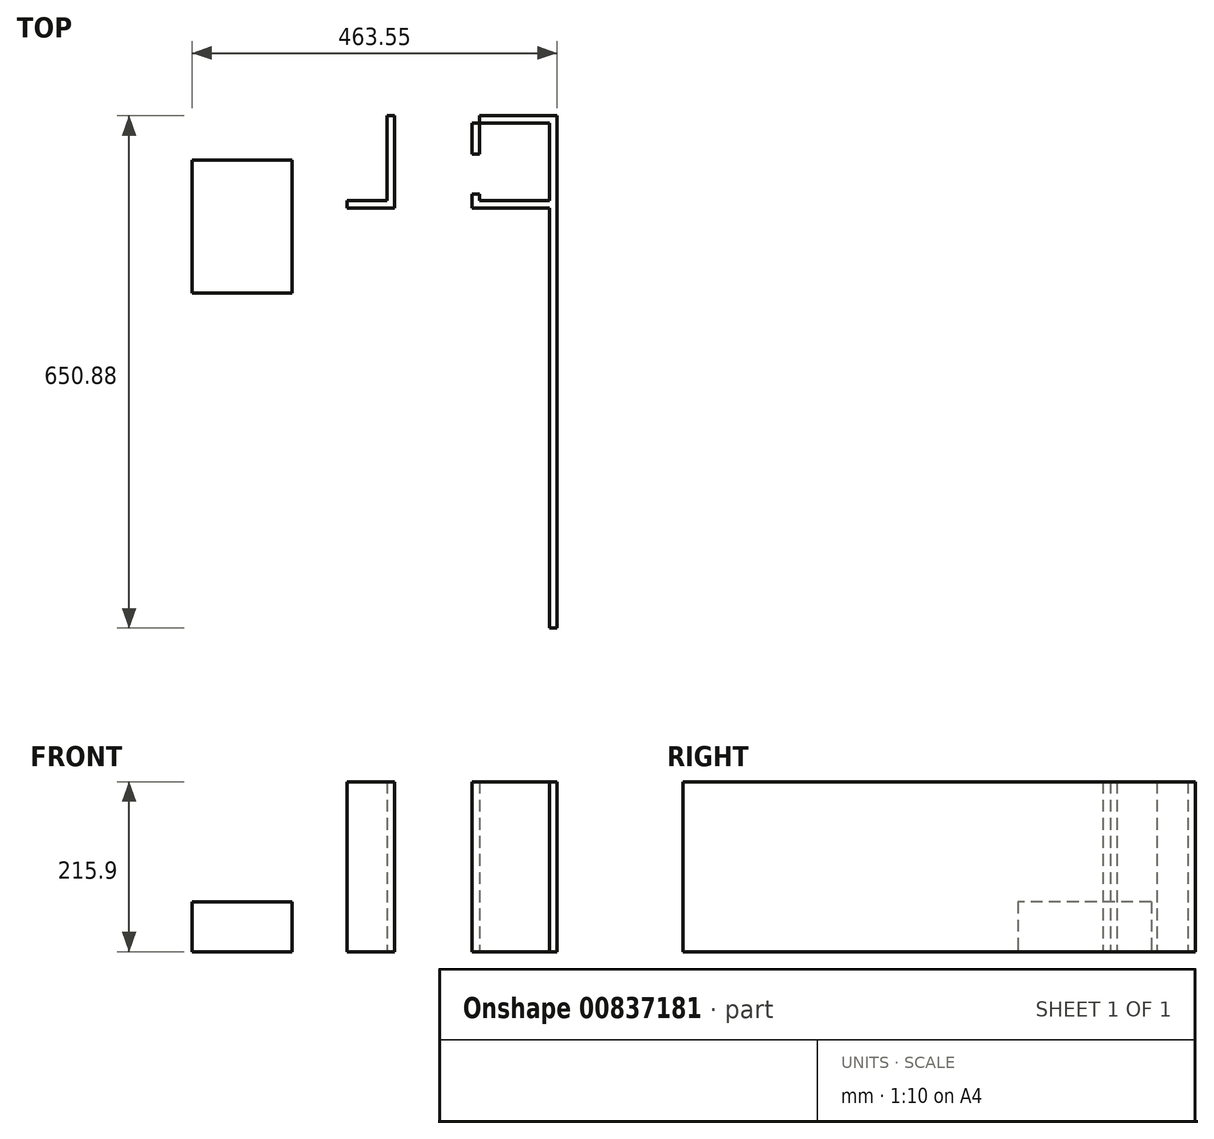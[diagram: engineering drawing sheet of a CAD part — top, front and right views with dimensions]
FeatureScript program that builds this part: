
annotation { "Feature Type Name" : "Feature", "Feature Type Description" : "" }
export const myFeature = defineFeature(function(context is Context, id is Id, definition is map)
    precondition{}
    {
        {
            var Q0;
            Q0=qCreatedBy(makeId("Top.planeOp"),FACE);
            var sketch = newSketch(context, id + "F0", { "sketchPlane" : qUnion([Q0])});
            skLineSegment(sketch, "E0.bottom", {"start": v(0, 0) * mm, "end": v(457.2, 0) * mm});
            skLineSegment(sketch, "E0.left", {"start": v(0, 0) * mm, "end": v(0, 203.2) * mm});
            skLineSegment(sketch, "E1.bottom", {"start": v(0, 0) * mm, "end": v(139.7, 0) * mm});
            skLineSegment(sketch, "E1.top", {"start": v(0, 203.2) * mm, "end": v(139.7, 203.2) * mm});
            skLineSegment(sketch, "E1.left", {"start": v(0, 25.4) * mm, "end": v(0, 203.2) * mm});
            skLineSegment(sketch, "E1.right", {"start": v(139.7, 0) * mm, "end": v(139.7, 25.4) * mm});
            skLineSegment(sketch, "E2.bottom", {"start": v(139.7, 203.2) * mm, "end": v(0, 203.2) * mm});
            skLineSegment(sketch, "E2.top", {"start": v(139.7, 415.93) * mm, "end": v(0, 415.93) * mm});
            skLineSegment(sketch, "E2.left", {"start": v(139.7, 212.72) * mm, "end": v(139.7, 348.2) * mm});
            skLineSegment(sketch, "E2.right", {"start": v(0, 212.72) * mm, "end": v(0, 415.93) * mm});
            skLineSegment(sketch, "E3.bottom", {"start": v(0, 415.93) * mm, "end": v(139.7, 415.93) * mm});
            skLineSegment(sketch, "E3.top", {"start": v(0, 425.45) * mm, "end": v(139.7, 425.45) * mm});
            skLineSegment(sketch, "E4.bottom", {"start": v(139.7, 425.45) * mm, "end": v(0, 425.45) * mm});
            skLineSegment(sketch, "E4.top", {"start": v(139.7, 594.78) * mm, "end": v(0, 594.78) * mm});
            skLineSegment(sketch, "E4.right", {"start": v(0, 425.45) * mm, "end": v(0, 594.78) * mm});
            skLineSegment(sketch, "E5.top", {"start": v(139.7, 212.72) * mm, "end": v(0, 212.72) * mm});
            skLineSegment(sketch, "E6.top", {"start": v(0, 25.4) * mm, "end": v(454.02, 25.4) * mm});
            skLineSegment(sketch, "E6.left", {"start": v(0, 0) * mm, "end": v(0, 25.4) * mm});
            skLineSegment(sketch, "E7.top", {"start": v(0, 0) * mm, "end": v(-9.53, 0) * mm});
            skLineSegment(sketch, "E7.left", {"start": v(0, 594.78) * mm, "end": v(0, 212.72) * mm});
            skLineSegment(sketch, "E7.right", {"start": v(-9.53, 594.78) * mm, "end": v(-9.53, 0) * mm});
            skLineSegment(sketch, "E8.top", {"start": v(0, 594.78) * mm, "end": v(139.7, 594.78) * mm});
            skLineSegment(sketch, "E9.top", {"start": v(-9.53, 604.3) * mm, "end": v(139.7, 604.3) * mm});
            skLineSegment(sketch, "E9.left", {"start": v(-9.53, 594.78) * mm, "end": v(-9.53, 604.3) * mm});
            skLineSegment(sketch, "E10.trimOffspring", {"start": v(139.7, 348.2) * mm, "end": v(139.7, 212.72) * mm});
            skLineSegment(sketch, "E11.trimOffspring", {"start": v(139.7, 25.4) * mm, "end": v(139.7, 0) * mm});
            skLineSegment(sketch, "E12.trimOffspring", {"start": v(0, 212.72) * mm, "end": v(0, 594.78) * mm});
            skLineSegment(sketch, "E13.trimOffspring", {"start": v(0, 203.2) * mm, "end": v(0, 25.4) * mm});
            skLineSegment(sketch, "E14", {"start": v(139.7, 604.3) * mm, "end": v(139.7, 650.88) * mm});
            skLineSegment(sketch, "E15", {"start": v(139.7, 650.88) * mm, "end": v(454.02, 650.88) * mm});
            skLineSegment(sketch, "E16.bottom", {"start": v(454.02, 650.88) * mm, "end": v(463.55, 650.88) * mm});
            skLineSegment(sketch, "E16.top", {"start": v(454.02, 0) * mm, "end": v(463.55, 0) * mm});
            skLineSegment(sketch, "E16.left", {"start": v(454.02, 650.88) * mm, "end": v(454.02, 0) * mm});
            skLineSegment(sketch, "E16.right", {"start": v(463.55, 650.88) * mm, "end": v(463.55, 0) * mm});
            skLineSegment(sketch, "E17.bottom", {"start": v(149.22, 641.35) * mm, "end": v(247.65, 641.35) * mm});
            skLineSegment(sketch, "E17.top", {"start": v(196.85, 542.92) * mm, "end": v(247.65, 542.92) * mm});
            skLineSegment(sketch, "E17.left", {"start": v(149.22, 641.35) * mm, "end": v(149.22, 594.78) * mm});
            skLineSegment(sketch, "E17.right", {"start": v(247.65, 641.35) * mm, "end": v(247.65, 542.93) * mm});
            skLineSegment(sketch, "E18.bottom", {"start": v(454.02, 641.35) * mm, "end": v(355.6, 641.35) * mm});
            skLineSegment(sketch, "E18.top", {"start": v(454.02, 542.93) * mm, "end": v(355.6, 542.93) * mm});
            skLineSegment(sketch, "E18.left", {"start": v(454.02, 641.35) * mm, "end": v(454.02, 542.93) * mm});
            skLineSegment(sketch, "E18.right", {"start": v(355.6, 641.35) * mm, "end": v(355.6, 542.93) * mm});
            skLineSegment(sketch, "E19.top", {"start": v(196.85, 533.4) * mm, "end": v(247.65, 533.4) * mm});
            skLineSegment(sketch, "E19.right", {"start": v(247.65, 542.93) * mm, "end": v(247.65, 533.4) * mm});
            skLineSegment(sketch, "E20.bottom", {"start": v(355.6, 542.93) * mm, "end": v(454.02, 542.93) * mm});
            skLineSegment(sketch, "E20.top", {"start": v(355.6, 533.4) * mm, "end": v(454.02, 533.4) * mm});
            skLineSegment(sketch, "E20.left", {"start": v(355.6, 542.93) * mm, "end": v(355.6, 533.4) * mm});
            skLineSegment(sketch, "E20.right", {"start": v(454.02, 542.93) * mm, "end": v(454.02, 533.4) * mm});
            skLineSegment(sketch, "E21.bottom", {"start": v(247.65, 533.4) * mm, "end": v(257.17, 533.4) * mm});
            skLineSegment(sketch, "E21.top", {"start": v(247.65, 650.88) * mm, "end": v(257.17, 650.88) * mm});
            skLineSegment(sketch, "E21.left", {"start": v(247.65, 533.4) * mm, "end": v(247.65, 650.88) * mm});
            skLineSegment(sketch, "E21.right", {"start": v(257.17, 533.4) * mm, "end": v(257.17, 650.88) * mm});
            skLineSegment(sketch, "E22.bottom", {"start": v(365.12, 533.4) * mm, "end": v(355.6, 533.4) * mm});
            skLineSegment(sketch, "E22.top", {"start": v(365.12, 650.88) * mm, "end": v(355.6, 650.88) * mm});
            skLineSegment(sketch, "E22.left", {"start": v(355.6, 533.4) * mm, "end": v(355.6, 650.88) * mm});
            skLineSegment(sketch, "E22.right", {"start": v(365.12, 533.4) * mm, "end": v(365.12, 650.88) * mm});
            skLineSegment(sketch, "E23", {"start": v(139.7, 425.45) * mm, "end": v(149.22, 425.45) * mm});
            skLineSegment(sketch, "E24", {"start": v(139.7, 415.93) * mm, "end": v(149.22, 415.93) * mm});
            skLineSegment(sketch, "E25", {"start": v(139.7, 348.2) * mm, "end": v(149.22, 348.2) * mm});
            skLineSegment(sketch, "E26", {"start": v(139.7, 177.8) * mm, "end": v(149.22, 177.8) * mm});
            skLineSegment(sketch, "E27.trimOffspring", {"start": v(139.7, 177.8) * mm, "end": v(139.7, 203.2) * mm});
            skLineSegment(sketch, "E28.trimOffspring", {"start": v(149.22, 348.2) * mm, "end": v(149.22, 177.8) * mm});
            skLineSegment(sketch, "E29.trimOffspring", {"start": v(149.22, 425.45) * mm, "end": v(149.22, 415.93) * mm});
            skLineSegment(sketch, "E30", {"start": v(139.7, 594.78) * mm, "end": v(149.22, 594.78) * mm});
            skLineSegment(sketch, "E31", {"start": v(196.85, 542.93) * mm, "end": v(196.85, 533.4) * mm});
            skLineSegment(sketch, "E32.bottom", {"start": v(365.12, 551.4) * mm, "end": v(355.6, 551.4) * mm});
            skLineSegment(sketch, "E32.top", {"start": v(365.12, 602.2) * mm, "end": v(355.6, 602.2) * mm});
            skLineSegment(sketch, "E32.left", {"start": v(365.12, 551.4) * mm, "end": v(365.12, 602.2) * mm});
            skLineSegment(sketch, "E32.right", {"start": v(355.6, 551.4) * mm, "end": v(355.6, 602.2) * mm});
            skSolve(sketch);
        }
        {
            var Q0;
            Q0=makeQuery(id+"F0.imprint","IMPRINT",FACE,{"disambiguationData":[TD([[makeQuery(id+"F0.imprint","IMPRINT",EDGE,{"derivedFrom":sQuery(id+"F0.wireOp",EDGE,"E2.bottom")}),-1.0]])]});
            var Q1;
            {var subQ1=sQuery(id+"F0.wireOp",EDGE,"E3.bottom");Q1=makeQuery(id+"F0.imprint","IMPRINT",FACE,{"disambiguationData":[TD([[makeQuery(id+"F0.imprint","IMPRINT",EDGE,{"derivedFrom":subQ1}),1.0]])]});}
            var Q2;
            {var subQ3=sQuery(id+"F0.wireOp",EDGE,"E21.bottom");Q2=makeQuery(id+"F0.imprint","IMPRINT",FACE,{"disambiguationData":[TD([[makeQuery(id+"F0.imprint","IMPRINT",EDGE,{"derivedFrom":subQ3}),1.0]])]});}
            var Q3;
            {var subQ0=sQuery(id+"F0.wireOp",EDGE,"E17.top");Q3=makeQuery(id+"F0.imprint","IMPRINT",FACE,{"disambiguationData":[TD([[makeQuery(id+"F0.imprint","IMPRINT",EDGE,{"derivedFrom":subQ0}),-1.0]])]});}
            var Q4;
            {var subQ5=sQuery(id+"F0.wireOp",EDGE,"E32.top");Q4=makeQuery(id+"F0.imprint","IMPRINT",FACE,{"disambiguationData":[TD([[makeQuery(id+"F0.imprint","IMPRINT",EDGE,{"derivedFrom":subQ5}),-1.0]])]});}
            var Q5;
            {var subQ5=sQuery(id+"F0.wireOp",EDGE,"E22.top");Q5=makeQuery(id+"F0.imprint","IMPRINT",FACE,{"disambiguationData":[TD([[makeQuery(id+"F0.imprint","IMPRINT",EDGE,{"derivedFrom":subQ5}),1.0]])]});}
            var Q6;
            {var subQ3=sQuery(id+"F0.wireOp",EDGE,"E22.right");var subQ5=sQuery(id+"F0.wireOp",EDGE,"E18.bottom");var subQ7=makeQuery(id+"F0.imprint","INTERSECT",VERTEX,{"derivedFrom":[subQ5,subQ3]});Q6=makeQuery(id+"F0.imprint","IMPRINT",FACE,{"disambiguationData":[TD([[makeQuery(id+"F0.imprint","IMPRINT",EDGE,{"disambiguationData":[TD([[subQ7,1.0]])],"derivedFrom":subQ5}),-1.0]])]});}
            var Q7;
            {var subQ3=sQuery(id+"F0.wireOp",EDGE,"E16.bottom");Q7=makeQuery(id+"F0.imprint","IMPRINT",FACE,{"disambiguationData":[TD([[makeQuery(id+"F0.imprint","IMPRINT",EDGE,{"derivedFrom":subQ3}),-1.0]])]});}
            var Q8;
            {var subQ4=sQuery(id+"F0.wireOp",EDGE,"E20.top");Q8=makeQuery(id+"F0.imprint","IMPRINT",FACE,{"disambiguationData":[TD([[makeQuery(id+"F0.imprint","IMPRINT",EDGE,{"derivedFrom":subQ4}),1.0]])]});}
            var Q9;
            {var subQ5=sQuery(id+"F0.wireOp",EDGE,"E32.bottom");Q9=makeQuery(id+"F0.imprint","IMPRINT",FACE,{"disambiguationData":[TD([[makeQuery(id+"F0.imprint","IMPRINT",EDGE,{"derivedFrom":subQ5}),1.0]])]});}
            var Q10;
            {var subQ5=sQuery(id+"F0.wireOp",EDGE,"E22.bottom");Q10=makeQuery(id+"F0.imprint","IMPRINT",FACE,{"disambiguationData":[TD([[makeQuery(id+"F0.imprint","IMPRINT",EDGE,{"derivedFrom":subQ5}),-1.0]])]});}
            var Q11;
            {var subQ3=sQuery(id+"F0.wireOp",EDGE,"E11.trimOffspring");Q11=makeQuery(id+"F0.imprint","IMPRINT",FACE,{"disambiguationData":[TD([[makeQuery(id+"F0.imprint","IMPRINT",EDGE,{"derivedFrom":subQ3}),1.0]])]});}
            var Q12;
            {var subQ0=sQuery(id+"F0.wireOp",EDGE,"E6.left");Q12=makeQuery(id+"F0.imprint","IMPRINT",FACE,{"disambiguationData":[TD([[makeQuery(id+"F0.imprint","IMPRINT",EDGE,{"derivedFrom":subQ0}),-1.0]])]});}
            extrude(context, id + "F1", {"entities" : qUnion([Q0, Q1, Q2, Q3, Q4, Q5, Q6, Q7, Q8, Q9, Q10, Q11, Q12]), "depth" : 215.9 * mm, "offsetDistance" : 25.4 * mm});
        }
        {
            var Q0;
            Q0=qCreatedBy(makeId("Top.planeOp"),FACE);
            var sketch = newSketch(context, id + "F2", { "sketchPlane" : qUnion([Q0])});
            skPoint(sketch, "E33.0", {"position": v(463.55, 650.88) * mm});
            skPoint(sketch, "E34.0", {"position": v(-9.53, 0) * mm});
            skLineSegment(sketch, "E35.bottom", {"start": v(-9.53, 0) * mm, "end": v(463.55, 0) * mm});
            skLineSegment(sketch, "E35.top", {"start": v(149.22, 650.88) * mm, "end": v(463.55, 650.88) * mm});
            skLineSegment(sketch, "E35.left", {"start": v(-9.53, 0) * mm, "end": v(-9.53, 594.78) * mm});
            skLineSegment(sketch, "E35.right", {"start": v(463.55, 0) * mm, "end": v(463.55, 650.88) * mm});
            skPoint(sketch, "E36.0", {"position": v(196.85, 542.92) * mm});
            skPoint(sketch, "E37.0", {"position": v(149.22, 594.78) * mm});
            skLineSegment(sketch, "E38", {"start": v(149.22, 594.78) * mm, "end": v(196.85, 594.78) * mm, "construction": true});
            skLineSegment(sketch, "E39", {"start": v(196.85, 594.78) * mm, "end": v(196.85, 542.92) * mm, "construction": true});
            skLineSegment(sketch, "E40.top", {"start": v(-9.53, 594.78) * mm, "end": v(149.22, 594.78) * mm});
            skLineSegment(sketch, "E40.right", {"start": v(149.22, 650.88) * mm, "end": v(149.22, 594.78) * mm});
            skSolve(sketch);
        }
        {
            var Q0;
            Q0=makeQuery(id+"F2.imprint","IMPRINT",FACE,{"disambiguationData":[TD([[makeQuery(id+"F2.imprint","IMPRINT",EDGE,{"derivedFrom":sQuery(id+"F2.wireOp",EDGE,"E35.bottom")}),1.0]])]});
            var sketch = newSketch(context, id + "F3", { "sketchPlane" : qUnion([Q0])});
            skPoint(sketch, "E41.0", {"position": v(0, 594.78) * mm});
            skLineSegment(sketch, "E42.bottom", {"start": v(0, 594.78) * mm, "end": v(127, 594.78) * mm});
            skLineSegment(sketch, "E42.top", {"start": v(0, 425.45) * mm, "end": v(127, 425.45) * mm});
            skLineSegment(sketch, "E42.left", {"start": v(0, 594.78) * mm, "end": v(0, 425.45) * mm});
            skLineSegment(sketch, "E42.right", {"start": v(127, 594.78) * mm, "end": v(127, 425.45) * mm});
            skSolve(sketch);
        }
        {
            var Q0;
            Q0 = qSketchRegion(id + "F3", true);
            extrude(context, id + "F4", {"entities" : qUnion([Q0]), "depth" : 63.5 * mm, "offsetDistance" : 25.4 * mm});
        }
    });
